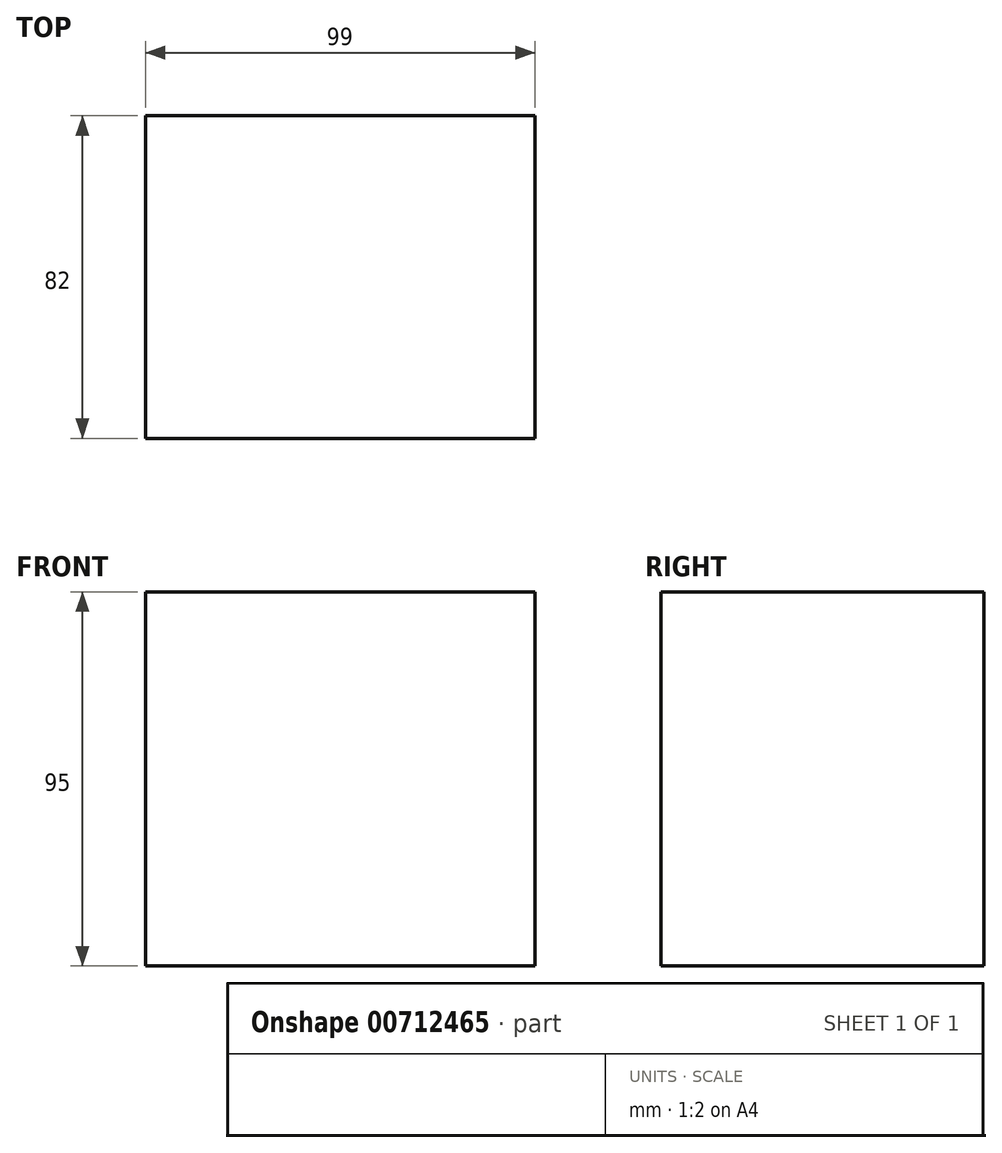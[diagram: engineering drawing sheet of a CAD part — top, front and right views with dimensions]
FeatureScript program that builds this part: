
annotation { "Feature Type Name" : "Feature", "Feature Type Description" : "" }
export const myFeature = defineFeature(function(context is Context, id is Id, definition is map)
    precondition{}
    {
        {
            var Q0;
            Q0=qCreatedBy(makeId("Top.planeOp"),FACE);
            var sketch = newSketch(context, id + "F0", { "sketchPlane" : qUnion([Q0])});
            skLineSegment(sketch, "E0.bottom", {"start": v(49.5, -41) * mm, "end": v(-49.5, -41) * mm});
            skLineSegment(sketch, "E0.top", {"start": v(49.5, 41) * mm, "end": v(-49.5, 41) * mm});
            skLineSegment(sketch, "E0.left", {"start": v(49.5, -41) * mm, "end": v(49.5, 41) * mm});
            skLineSegment(sketch, "E0.right", {"start": v(-49.5, -41) * mm, "end": v(-49.5, 41) * mm});
            skPoint(sketch, "E0.middle", {"position": v(0, 0) * mm});
            skSolve(sketch);
        }
        {
            var Q0;
            Q0 = qSketchRegion(id + "F0", true);
            extrude(context, id + "F1", {"entities" : qUnion([Q0]), "endBound" : BoundingType.SYMMETRIC, "depth" : 95 * mm, "offsetDistance" : 25 * mm});
        }
    });
